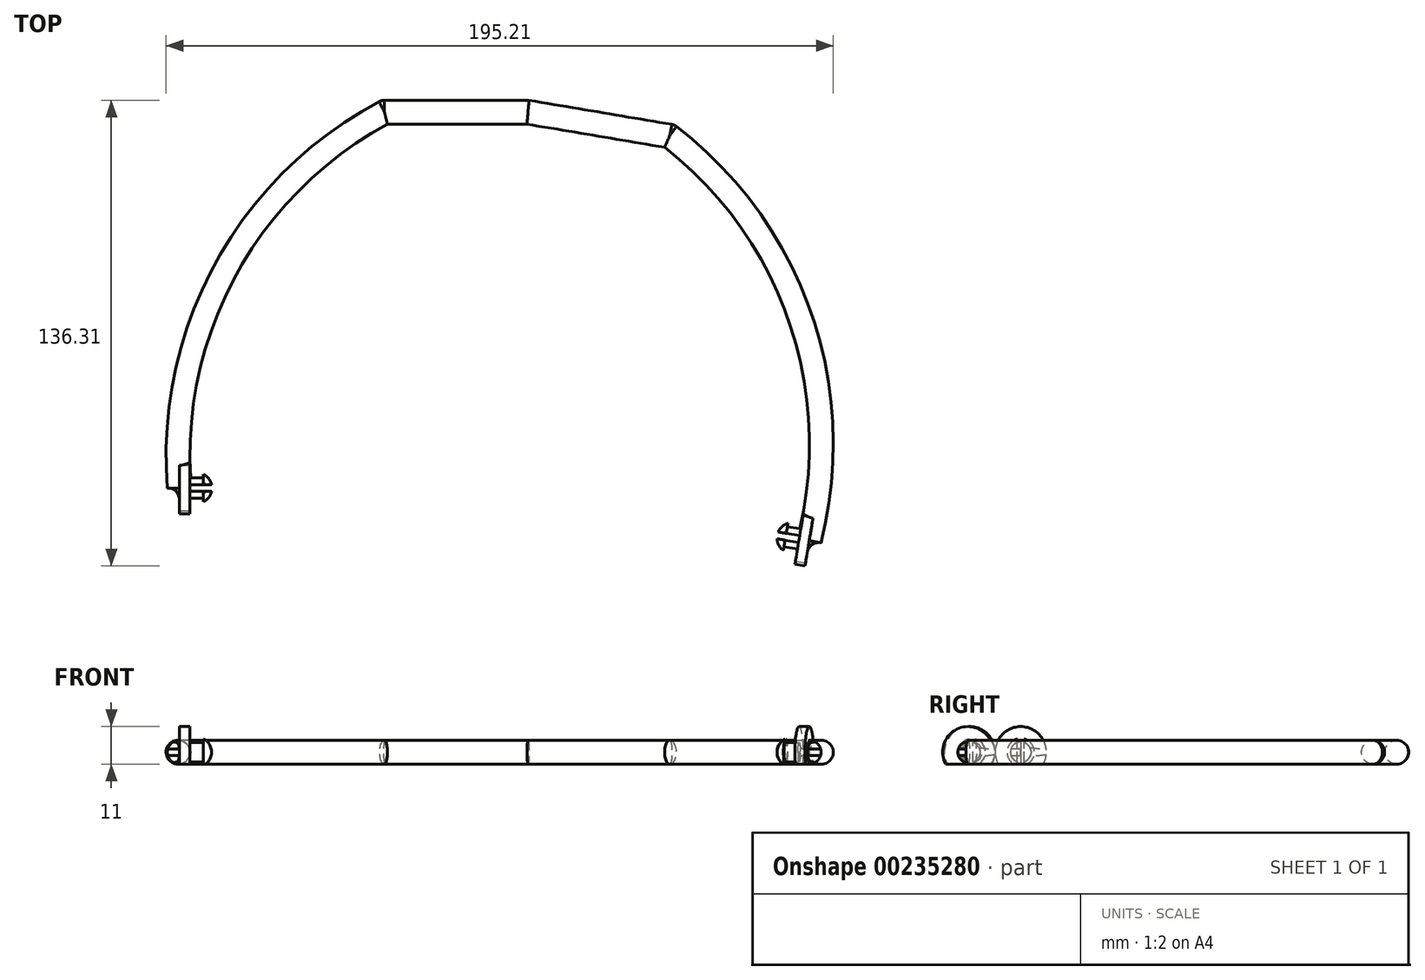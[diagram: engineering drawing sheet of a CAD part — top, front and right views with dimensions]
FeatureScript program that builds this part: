
annotation { "Feature Type Name" : "Feature", "Feature Type Description" : "" }
export const myFeature = defineFeature(function(context is Context, id is Id, definition is map)
    precondition{}
    {
        {
            var Q0;
            Q0=qCreatedBy(makeId("Top.planeOp"),FACE);
            var sketch = newSketch(context, id + "F0", { "sketchPlane" : qUnion([Q0])});
            skArc(sketch, "E0", {"start": v(60, 110) * mm, "mid": v(13.5, 64) * mm, "end": v(0, 0) * mm});
            skLineSegment(sketch, "E1", {"start": v(60, 110) * mm, "end": v(102, 110) * mm});
            skSolve(sketch);
        }
        {
            var Q0;
            Q0=qCreatedBy(makeId("Front.planeOp"),FACE);
            var sketch = newSketch(context, id + "F1", { "sketchPlane" : qUnion([Q0])});
            skCircle(sketch, "E2", {"center": v(0, 0) * mm, "radius": 3.5 * mm});
            skSolve(sketch);
        }
        {
            var Q0;
            Q0=makeQuery(id+"F1.imprint","IMPRINT",FACE,{"disambiguationData":[TD([[makeQuery(id+"F1.imprint","IMPRINT",EDGE,{"derivedFrom":sQuery(id+"F1.wireOp",EDGE,"E2")}),1.0]])]});
            var Q1;
            Q1=sQuery(id+"F0.wireOp",EDGE,"E0");
            var Q2;
            Q2=sQuery(id+"F0.wireOp",EDGE,"E1");
            sweep(context, id + "F2", {"profiles" : qUnion([Q0]), "path" : qUnion([Q1, Q2])});
        }
        {
            var Q0;
            Q0=qCreatedBy(makeId("Right.planeOp"),FACE);
            var sketch = newSketch(context, id + "F3", { "sketchPlane" : qUnion([Q0])});
            skCircle(sketch, "E3", {"center": v(0, 0) * mm, "radius": 3 * mm});
            skSolve(sketch);
        }
        {
            var Q0;
            Q0=makeQuery(id+"F3.imprint","IMPRINT",FACE,{"disambiguationData":[TD([[makeQuery(id+"F3.imprint","IMPRINT",EDGE,{"derivedFrom":sQuery(id+"F3.wireOp",EDGE,"E3")}),1.0]])]});
            extrude(context, id + "F4", {"entities" : qUnion([Q0]), "operationType" : NewBodyOperationType.ADD, "depth" : 7 * mm});
        }
        {
            var Q0;
            Q0=qCreatedBy(makeId("Front.planeOp"),FACE);
            var sketch = newSketch(context, id + "F5", { "sketchPlane" : qUnion([Q0])});
            skLineSegment(sketch, "E4", {"start": v(9.5, 0) * mm, "end": v(7, 0) * mm});
            skLineSegment(sketch, "E5", {"start": v(7, 0) * mm, "end": v(7, -4) * mm});
            skArc(sketch, "E6", {"start": v(7, -4) * mm, "mid": v(8.85, -2.38) * mm, "end": v(9.5, 0) * mm});
            skSolve(sketch);
        }
        {
            var Q0;
            Q0=makeQuery(id+"F5.imprint","IMPRINT",FACE,{"disambiguationData":[TD([[makeQuery(id+"F5.imprint","IMPRINT",EDGE,{"derivedFrom":sQuery(id+"F5.wireOp",EDGE,"E4")}),1.0]])]});
            var Q1;
            Q1=sQuery(id+"F5.wireOp",EDGE,"E4");
            revolve(context, id + "F6", {"operationType" : NewBodyOperationType.ADD, "entities" : qUnion([Q0]), "axis" : qUnion([Q1]), "revolveType" : RevolveType.FULL});
        }
        {
            var Q0;
            Q0=qCreatedBy(makeId("Top.planeOp"),FACE);
            var sketch = newSketch(context, id + "F7", { "sketchPlane" : qUnion([Q0])});
            skLineSegment(sketch, "E7.bottom", {"start": v(3.01, 1) * mm, "end": v(10.01, 1) * mm});
            skLineSegment(sketch, "E7.top", {"start": v(3.01, 0) * mm, "end": v(10.01, 0) * mm});
            skLineSegment(sketch, "E7.left", {"start": v(3.01, 1) * mm, "end": v(3.01, 0) * mm});
            skLineSegment(sketch, "E7.right", {"start": v(10.01, 1) * mm, "end": v(10.01, 0) * mm});
            skLineSegment(sketch, "E8.MirrorCS", {"start": v(3.01, -1) * mm, "end": v(10.01, -1) * mm});
            skLineSegment(sketch, "E9.MirrorCS", {"start": v(3.01, -1) * mm, "end": v(3.01, 0) * mm});
            skLineSegment(sketch, "E10.MirrorCS", {"start": v(10.01, -1) * mm, "end": v(10.01, 0) * mm});
            skSolve(sketch);
        }
        {
            var Q0;
            Q0=makeQuery(id+"F7.imprint","IMPRINT",FACE,{"disambiguationData":[TD([[makeQuery(id+"F7.imprint","IMPRINT",EDGE,{"derivedFrom":sQuery(id+"F7.wireOp",EDGE,"E7.bottom")}),-1.0]])]});
            var Q1;
            Q1=makeQuery(id+"F7.imprint","IMPRINT",FACE,{"disambiguationData":[TD([[makeQuery(id+"F7.imprint","IMPRINT",EDGE,{"derivedFrom":sQuery(id+"F7.wireOp",EDGE,"E7.top")}),-1.0]])]});
            extrude(context, id + "F8", {"entities" : qUnion([Q0, Q1]), "operationType" : NewBodyOperationType.REMOVE, "endBound" : BoundingType.SYMMETRIC, "oppositeDirection" : true, "depth" : 10 * mm});
        }
        {
            var Q0;
            Q0=makeQuery(id+"F8.boolean.opBoolean","COPY",FACE,{"derivedFrom":makeQuery(id+"F8.opExtrude","SWEPT_FACE",FACE,{"disambiguationData":[OSD([sQuery(id+"F7.wireOp",EDGE,"E7.left"),sQuery(id+"F7.wireOp",EDGE,"E9.MirrorCS")])]})});
            var sketch = newSketch(context, id + "F9", { "sketchPlane" : qUnion([Q0])});
            skCircle(sketch, "E11", {"center": v(0, 0) * mm, "radius": 7.5 * mm});
            skSolve(sketch);
        }
        {
            var Q0;
            Q0=makeQuery(id+"F9.imprint","IMPRINT",FACE,{"disambiguationData":[TD([[makeQuery(id+"F9.imprint","IMPRINT",EDGE,{"derivedFrom":sQuery(id+"F9.wireOp",EDGE,"E11")}),1.0]])]});
            extrude(context, id + "F10", {"entities" : qUnion([Q0]), "operationType" : NewBodyOperationType.ADD, "oppositeDirection" : true, "depth" : 3 * mm});
        }
        {
            var Q0;
            Q0=makeQuery(id+"F4.boolean.opBoolean","INTERSECT",EDGE,{"derivedFrom":[makeQuery(id+"F2.opSweep","CAP_FACE",FACE,{"disambiguationData":[OSD([sQuery(id+"F0.wireOp",VERTEX,"E0.end"),sQuery(id+"F1.wireOp",EDGE,"E2")])],"isStart":true}),makeQuery(id+"F4.opExtrude","CAP_FACE",FACE,{"disambiguationData":[OSD([sQuery(id+"F3.wireOp",EDGE,"E3")])],"isStart":true})]});
            fillet(context, id + "F11", {"entities" : qUnion([Q0]), "radius" : 3.38 * mm, "tangentPropagation" : true, "allowEdgeOverflow" : false});
        }
        {
            var Q0;
            Q0=qCreatedBy(makeId("Front.planeOp"),FACE);
            var sketch = newSketch(context, id + "F12", { "sketchPlane" : qUnion([Q0])});
            skArc(sketch, "E12.0", {"start": v(1.8, -3) * mm, "mid": v(-3.5, 0) * mm, "end": v(1.8, 3) * mm});
            skLineSegment(sketch, "E13.bottom", {"start": v(0, -3.5) * mm, "end": v(13.75, -3.5) * mm});
            skLineSegment(sketch, "E13.top", {"start": v(0, -8.7) * mm, "end": v(13.75, -8.7) * mm});
            skLineSegment(sketch, "E13.left", {"start": v(0, -3.5) * mm, "end": v(0, -8.7) * mm});
            skLineSegment(sketch, "E13.right", {"start": v(13.75, -3.5) * mm, "end": v(13.75, -8.7) * mm});
            skSolve(sketch);
        }
        {
            var Q0;
            Q0=makeQuery(id+"F12.imprint","IMPRINT",FACE,{"disambiguationData":[TD([[makeQuery(id+"F12.imprint","IMPRINT",EDGE,{"derivedFrom":sQuery(id+"F12.wireOp",EDGE,"E13.bottom")}),-1.0]])]});
            extrude(context, id + "F13", {"entities" : qUnion([Q0]), "operationType" : NewBodyOperationType.REMOVE, "endBound" : BoundingType.SYMMETRIC, "oppositeDirection" : true, "depth" : 20 * mm});
        }
        {
            var Q0;
            Q0=makeQuery(id+"F2.opSweep","SWEPT_BODY",BODY,{"disambiguationData":[OSD([sQuery(id+"F0.wireOp",EDGE,"E1"),sQuery(id+"F1.wireOp",EDGE,"E2")])]});
            var Q1;
            Q1=makeQuery(id+"F2.opSweep","CAP_FACE",FACE,{"disambiguationData":[OSD([sQuery(id+"F0.wireOp",VERTEX,"E1.end"),sQuery(id+"F1.wireOp",EDGE,"E2")])],"isStart":false});
            mirror(context, id + "F14", {"operationType" : NewBodyOperationType.ADD, "entities" : qUnion([Q0]), "mirrorPlane" : qUnion([Q1])});
        }
        {
            var Q0;
            Q0=makeQuery(id+"F2.opSweep","MID_CAP_EDGE",EDGE,{"disambiguationData":[OSD([sQuery(id+"F0.wireOp",VERTEX,"E1.start"),sQuery(id+"F1.wireOp",EDGE,"E2")]),OD(1.0)],"capPos":1.0});
            var Q1;
            Q1=makeQuery(id+"F14.opPattern","COPY",EDGE,{"derivedFrom":makeQuery(id+"F2.opSweep","MID_CAP_EDGE",EDGE,{"disambiguationData":[OSD([sQuery(id+"F0.wireOp",VERTEX,"E1.start"),sQuery(id+"F1.wireOp",EDGE,"E2")]),OD(1.0)],"capPos":1.0}),"instanceName":"1"});
            fillet(context, id + "F15", {"entities" : qUnion([Q0, Q1]), "radius" : 3 * mm, "tangentPropagation" : true, "allowEdgeOverflow" : false});
        }
    });
